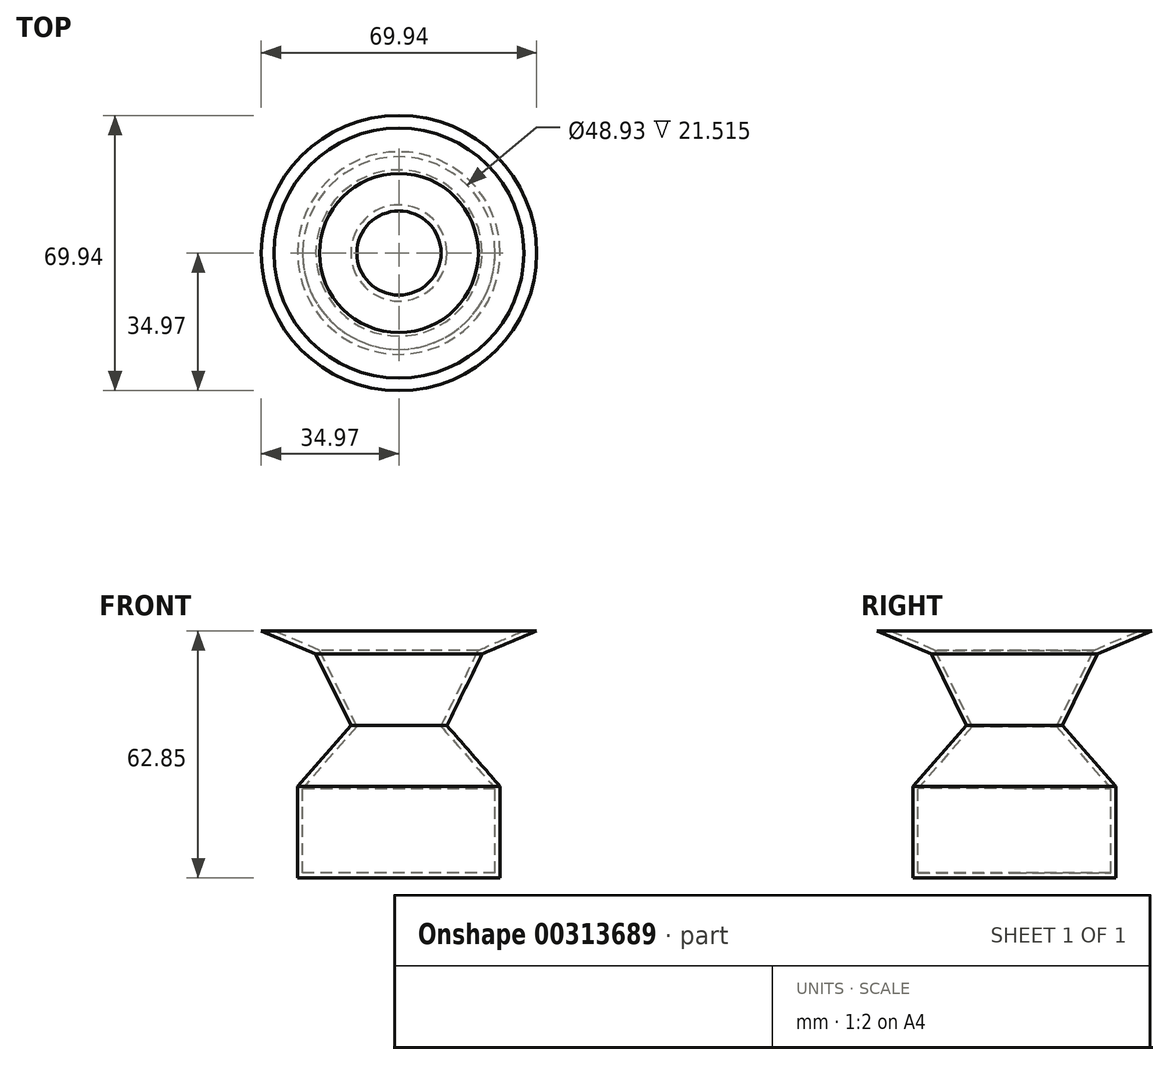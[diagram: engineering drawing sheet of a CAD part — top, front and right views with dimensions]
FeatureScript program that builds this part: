
annotation { "Feature Type Name" : "Feature", "Feature Type Description" : "" }
export const myFeature = defineFeature(function(context is Context, id is Id, definition is map)
    precondition{}
    {
        {
            var Q0;
            Q0=qCreatedBy(makeId("Front.planeOp"),FACE);
            var sketch = newSketch(context, id + "F0", { "sketchPlane" : qUnion([Q0])});
            skLineSegment(sketch, "E0", {"start": v(0, 0) * mm, "end": v(25.74, 0) * mm});
            skLineSegment(sketch, "E1", {"start": v(25.74, 0) * mm, "end": v(25.74, 23.26) * mm});
            skLineSegment(sketch, "E2", {"start": v(25.74, 23.26) * mm, "end": v(12.2, 38.77) * mm});
            skLineSegment(sketch, "E3", {"start": v(12.2, 38.77) * mm, "end": v(21.12, 56.91) * mm});
            skLineSegment(sketch, "E4", {"start": v(21.12, 56.91) * mm, "end": v(34.97, 62.85) * mm});
            skLineSegment(sketch, "E5", {"start": v(34.97, 62.85) * mm, "end": v(0, 62.85) * mm});
            skLineSegment(sketch, "E6", {"start": v(0, 62.85) * mm, "end": v(0, 0) * mm});
            skSolve(sketch);
        }
        {
            var Q0;
            Q0=makeQuery(id+"F0.imprint","IMPRINT",FACE,{"disambiguationData":[TD([[makeQuery(id+"F0.imprint","IMPRINT",EDGE,{"derivedFrom":sQuery(id+"F0.wireOp",EDGE,"E0")}),1.0]])]});
            var Q1;
            Q1=sQuery(id+"F0.wireOp",EDGE,"E6");
            revolve(context, id + "F1", {"entities" : qUnion([Q0]), "axis" : qUnion([Q1]), "revolveType" : RevolveType.FULL});
        }
        {
            var Q0;
            Q0=makeQuery(id+"F1.opRevolve","SWEPT_FACE",FACE,{"disambiguationData":[OSD([sQuery(id+"F0.wireOp",EDGE,"E5")])]});
            shell(context, id + "F2", {"entities" : qUnion([Q0]), "thickness" : 1.27 * mm});
        }
    });
